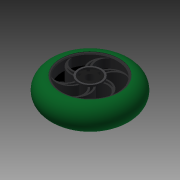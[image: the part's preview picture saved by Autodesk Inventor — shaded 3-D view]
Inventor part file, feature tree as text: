
AUTODESK INVENTOR PART (.ipt)
format: ipt  version: 2015 (Build 190159000, 159)  size: 858,624 bytes
history: native  units: in
note: dims shown in document units (in); Inventor stores cm internally (conversion verified against a paired STEP export)
features: sketch x14, extrude x11, mirror x6, sweep x1, chamfer x1, projected_geometry x1
ambient origin geometry x8: Origin, YZ Plane, XZ Plane, XY Plane, X Axis, Y Axis, Z Axis, Center Point
bodies: Solid1 (feature_tree)
feature tree (34):
  sweep  "Sweep1"
  sketch  "Sketch3"  dims[d18=0.0625in d19=0.0in d20=0.25in d21=0.0in]
  sketch  "Sketch6"  dims[d22=0.0625in d23=0.0in d24=0.0625in d25=0.0in]
  extrude  "Extrusion4"  Depth=1.75in
  extrude  "Extrusion5"  Depth=0.0625in TaperAngle=0.0deg
  extrude  "Extrusion6"  Depth=0.0625in TaperAngle=0.0deg
  mirror  "Mirror1"
  extrude  "Extrusion7"  Depth=0.24in TaperAngle=0.0deg
  mirror  "Mirror2"
  sketch  "Sketch11"  dims[d38=0.025in d39=0.125in d40=45.0deg d105=0.25in]
  extrude  "Extrusion8"  Depth=0.0625in TaperAngle=0.0deg
  extrude  "Extrusion9"  Depth=0.65in TaperAngle=0.0deg
  mirror  "Mirror3"
  extrude  "Extrusion10"  Depth=0.125in
  mirror  "Mirror4"
  extrude  "Extrusion11"  [1 undecoded]
  mirror  "Mirror5"
  extrude  "Extrusion12"  [1 undecoded]
  mirror  "Mirror6"
  extrude  "Extrusion13"  [1 undecoded]
  chamfer  "Chamfer1"  [1 undecoded]
  extrude  "Extrusion26"  [1 undecoded]
  sketch  "Sketch1"  dims[d0=2.5in d1=0.75in]
  sketch  "Sketch2"  dims[d2=0.0in d3=0.0in d4=1.75in]
  sketch  "Sketch7"  dims[d26=0.25in d27=0.0in d28=0.24in d29=0.0in]
  sketch  "Sketch9"  dims[d30=0.2in d31=0.0in d32=0.0625in d33=0.0in]
  sketch  "Sketch10"  dims[d34=0.05in d35=0.0in d36=0.65in d37=0.0in]
  sketch  "Sketch12"  dims[d106=1.0in d107=0.0in]
  sketch  "Sketch14"
  projected_geometry  "Projected Loop2"
  sketch  "Sketch15"
  sketch  "Sketch16"
  sketch  "Sketch18"
  sketch  "Sketch35"
note: 5 required parameter values undecoded (feature->parameter linkage not recoverable at this tier; creation-order binding heuristic only, values carry confidence <= 0.55)
